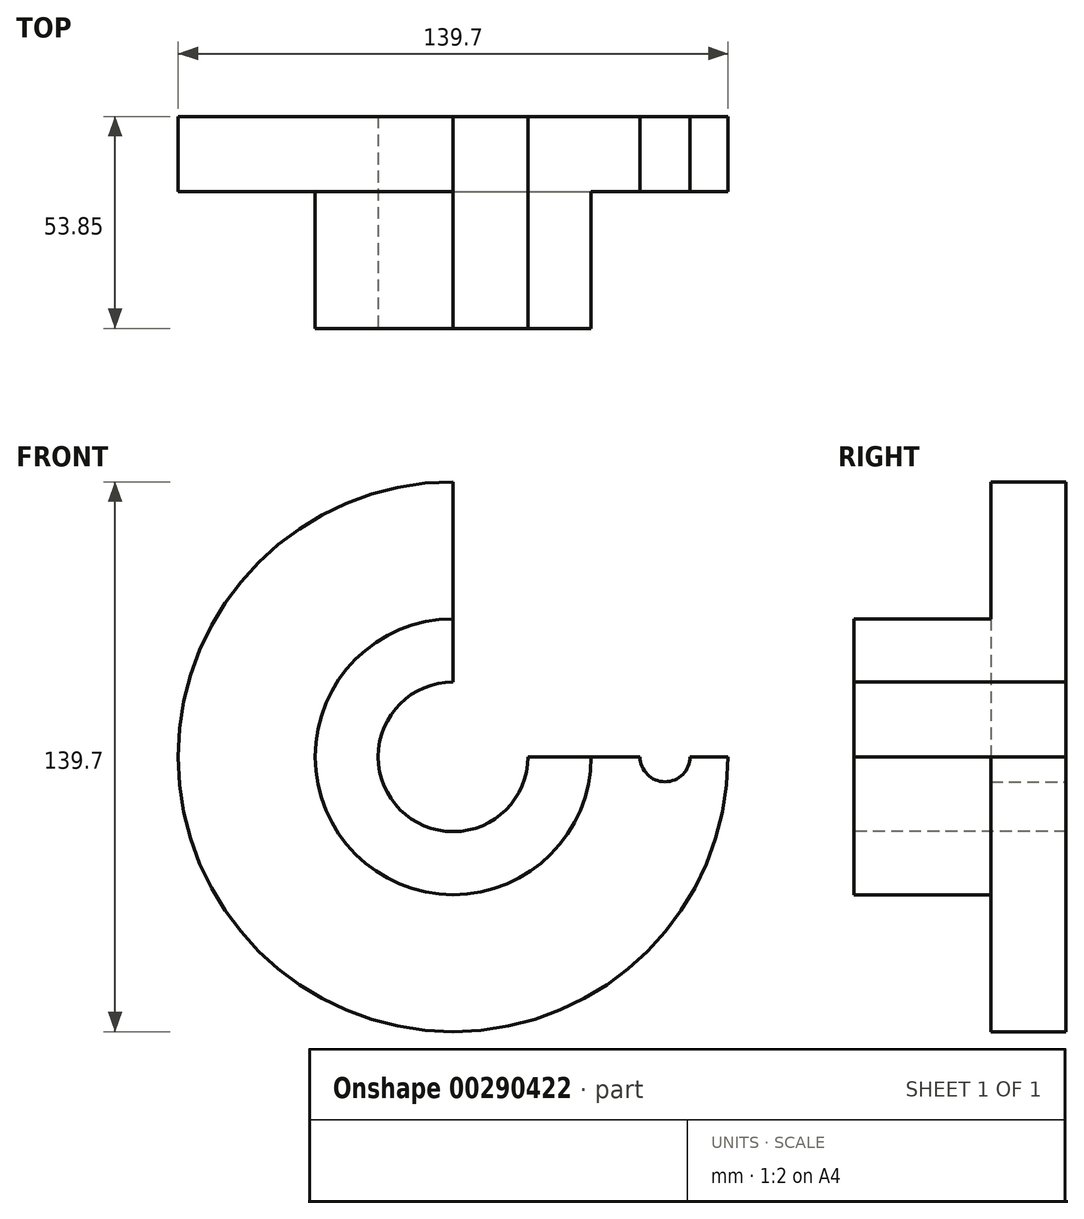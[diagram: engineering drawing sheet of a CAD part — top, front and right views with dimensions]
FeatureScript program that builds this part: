
annotation { "Feature Type Name" : "Feature", "Feature Type Description" : "" }
export const myFeature = defineFeature(function(context is Context, id is Id, definition is map)
    precondition{}
    {
        {
            var Q0;
            Q0=qCreatedBy(makeId("Top.planeOp"),FACE);
            var sketch = newSketch(context, id + "F0", { "sketchPlane" : qUnion([Q0])});
            skLineSegment(sketch, "E0", {"start": v(0, 0) * mm, "end": v(0, -53.85) * mm});
            skLineSegment(sketch, "E1", {"start": v(0, -53.85) * mm, "end": v(35.05, -53.85) * mm});
            skLineSegment(sketch, "E2", {"start": v(35.05, -53.85) * mm, "end": v(35.05, -19.05) * mm});
            skLineSegment(sketch, "E3", {"start": v(35.05, -19.05) * mm, "end": v(69.85, -19.05) * mm});
            skLineSegment(sketch, "E4", {"start": v(69.85, -19.05) * mm, "end": v(69.85, 0) * mm});
            skLineSegment(sketch, "E5", {"start": v(69.85, 0) * mm, "end": v(0, 0) * mm});
            skSolve(sketch);
        }
        {
            var Q0;
            Q0=makeQuery(id+"F0.imprint","IMPRINT",FACE,{"disambiguationData":[TD([[makeQuery(id+"F0.imprint","IMPRINT",EDGE,{"derivedFrom":sQuery(id+"F0.wireOp",EDGE,"E0")}),1.0]])]});
            var Q1;
            Q1=sQuery(id+"F0.wireOp",EDGE,"E0");
            revolve(context, id + "F1", {"entities" : qUnion([Q0]), "axis" : qUnion([Q1]), "revolveType" : RevolveType.ONE_DIRECTION, "oppositeDirection" : true, "angle" : 270 * degree});
        }
        {
            var Q0;
            Q0=makeQuery(id+"F1.opRevolve","SWEPT_FACE",FACE,{"disambiguationData":[OSD([sQuery(id+"F0.wireOp",EDGE,"E5")])]});
            var sketch = newSketch(context, id + "F2", { "sketchPlane" : qUnion([Q0])});
            skCircle(sketch, "E6", {"center": v(0, 0) * mm, "radius": 53.85 * mm});
            skCircle(sketch, "E7", {"center": v(-53.85, 0) * mm, "radius": 6.35 * mm});
            skCircle(sketch, "E8", {"center": v(0, 53.85) * mm, "radius": 6.35 * mm});
            skSolve(sketch);
        }
        {
            var Q0;
            {var subQ0=sQuery(id+"F2.wireOp",EDGE,"E7");var subQ1=sQuery(id+"F2.wireOp",EDGE,"E6");var subQ2=makeQuery(id+"F2.imprint","INTERSECT",VERTEX,{"disambiguationData":[OD(1.0)],"derivedFrom":[subQ1,subQ0]});Q0=makeQuery(id+"F2.imprint","IMPRINT",FACE,{"disambiguationData":[TD([[makeQuery(id+"F2.imprint","IMPRINT",EDGE,{"disambiguationData":[TD([[subQ2,1.0]])],"derivedFrom":subQ1}),-1.0]])]});}
            var Q1;
            {var subQ0=sQuery(id+"F2.wireOp",EDGE,"E7");var subQ1=sQuery(id+"F2.wireOp",EDGE,"E6");Q1=makeQuery(id+"F2.imprint","IMPRINT",FACE,{"disambiguationData":[TD([[makeQuery(id+"F2.imprint","IMPRINT",EDGE,{"disambiguationData":[TD([[makeQuery(id+"F2.imprint","INTERSECT",VERTEX,{"disambiguationData":[OD(1.0)],"derivedFrom":[subQ1,subQ0]}),1.0]])],"derivedFrom":subQ1}),1.0]])]});}
            var Q2;
            Q2=sQuery(id+"F2.wireOp",EDGE,"E7");
            extrude(context, id + "F3", {"entities" : qUnion([Q0, Q1]), "operationType" : NewBodyOperationType.REMOVE, "surfaceEntities" : qUnion([Q2]), "oppositeDirection" : true, "depth" : 25.4 * mm});
        }
        {
            var Q0;
            Q0=makeQuery(id+"F1.opRevolve","SWEPT_FACE",FACE,{"disambiguationData":[OSD([sQuery(id+"F0.wireOp",EDGE,"E1")])]});
            var sketch = newSketch(context, id + "F4", { "sketchPlane" : qUnion([Q0])});
            skCircle(sketch, "E9", {"center": v(0, 0) * mm, "radius": 19.02 * mm});
            skSolve(sketch);
        }
        {
            var Q0;
            {var subQ0=sQuery(id+"F4.wireOp",EDGE,"E9");var subQ1=sQuery(id+"F0.wireOp",EDGE,"E1");var subQ2=makeQuery(id+"F1.opRevolve","CAP_EDGE",EDGE,{"disambiguationData":[OSD([subQ1])],"isStart":true});var subQ3=makeQuery(id+"F4.imprint","INTERSECT",VERTEX,{"derivedFrom":[subQ2,subQ0]});Q0=makeQuery(id+"F4.imprint","IMPRINT",FACE,{"disambiguationData":[TD([[makeQuery(id+"F4.imprint","IMPRINT",EDGE,{"disambiguationData":[TD([[subQ3,1.0]])],"derivedFrom":subQ0}),1.0]])]});}
            var Q1;
            Q1=sQuery(id+"F4.wireOp",EDGE,"E9");
            extrude(context, id + "F5", {"entities" : qUnion([Q0]), "operationType" : NewBodyOperationType.REMOVE, "surfaceEntities" : qUnion([Q1]), "oppositeDirection" : true, "depth" : 76.2 * mm});
        }
    });
